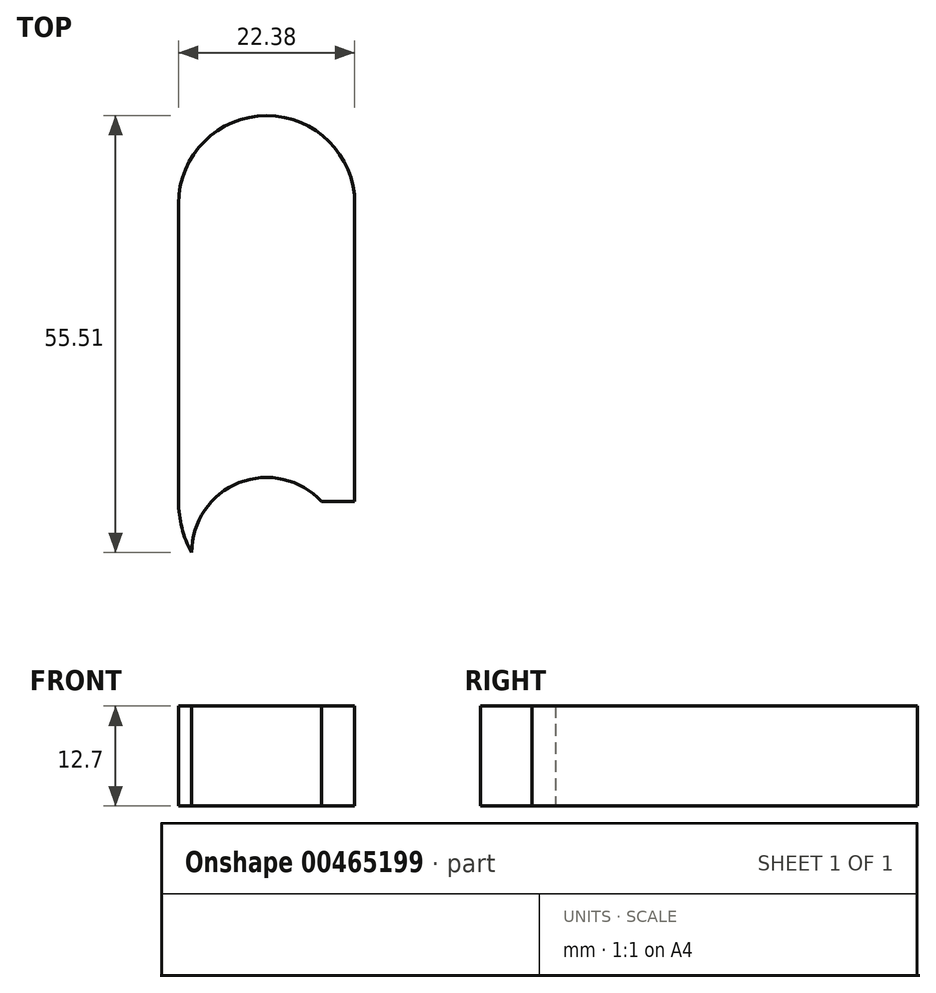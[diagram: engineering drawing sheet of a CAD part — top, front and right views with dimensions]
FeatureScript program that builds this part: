
annotation { "Feature Type Name" : "Feature", "Feature Type Description" : "" }
export const myFeature = defineFeature(function(context is Context, id is Id, definition is map)
    precondition{}
    {
        {
            var Q0;
            Q0=qCreatedBy(makeId("Top.planeOp"),FACE);
            var sketch = newSketch(context, id + "F0", { "sketchPlane" : qUnion([Q0])});
            skCircle(sketch, "E0", {"center": v(0, 0) * mm, "radius": 9.53 * mm});
            skLineSegment(sketch, "E1", {"start": v(0, 0) * mm, "end": v(0, 25.4) * mm});
            skLineSegment(sketch, "E2.bottom", {"start": v(11.2, 6.49) * mm, "end": v(-11.2, 6.49) * mm});
            skLineSegment(sketch, "E2.top", {"start": v(11.2, 44.31) * mm, "end": v(-11.2, 44.31) * mm});
            skLineSegment(sketch, "E2.left", {"start": v(11.2, 6.49) * mm, "end": v(11.2, 44.31) * mm});
            skLineSegment(sketch, "E2.right", {"start": v(-11.2, 6.49) * mm, "end": v(-11.2, 44.31) * mm});
            skPoint(sketch, "E2.middle", {"position": v(0, 25.4) * mm});
            skArc(sketch, "E3", {"start": v(-11.2, 44.31) * mm, "mid": v(0, 55.5) * mm, "end": v(11.2, 44.31) * mm});
            skArc(sketch, "E4", {"start": v(11.2, 6.49) * mm, "mid": v(10.77, 3.14) * mm, "end": v(9.53, 0) * mm});
            skArc(sketch, "E5", {"start": v(-11.2, 6.49) * mm, "mid": v(-10.77, 3.14) * mm, "end": v(-9.53, 0) * mm});
            skLineSegment(sketch, "E6", {"start": v(-8.84, -3.54) * mm, "end": v(-11.67, -9.3) * mm});
            skLineSegment(sketch, "E7", {"start": v(-11.67, -9.3) * mm, "end": v(-9.89, -15.42) * mm});
            skLineSegment(sketch, "E8", {"start": v(-9.89, -15.42) * mm, "end": v(-4.82, -8.22) * mm});
            skLineSegment(sketch, "E9", {"start": v(-4.82, -8.22) * mm, "end": v(4.82, -8.22) * mm});
            skLineSegment(sketch, "E10", {"start": v(4.82, -8.22) * mm, "end": v(7.67, -14.7) * mm});
            skLineSegment(sketch, "E11", {"start": v(7.67, -14.7) * mm, "end": v(11.12, -9.3) * mm});
            skLineSegment(sketch, "E12", {"start": v(11.12, -9.3) * mm, "end": v(9.53, 0) * mm});
            skLineSegment(sketch, "E13", {"start": v(-9.53, 0) * mm, "end": v(-11.67, -9.3) * mm});
            skSolve(sketch);
        }
        {
            var Q0;
            Q0=makeQuery(id+"F0.imprint","IMPRINT",FACE,{"disambiguationData":[TD([[makeQuery(id+"F0.imprint","IMPRINT",EDGE,{"derivedFrom":sQuery(id+"F0.wireOp",EDGE,"E2.top")}),-1.0]])]});
            var Q1;
            Q1=makeQuery(id+"F0.imprint","IMPRINT",FACE,{"disambiguationData":[TD([[makeQuery(id+"F0.imprint","IMPRINT",EDGE,{"derivedFrom":sQuery(id+"F0.wireOp",EDGE,"E2.top")}),1.0]])]});
            var Q2;
            {var subQ0=sQuery(id+"F0.wireOp",EDGE,"E4");Q2=makeQuery(id+"F0.imprint","IMPRINT",FACE,{"disambiguationData":[TD([[makeQuery(id+"F0.imprint","IMPRINT",EDGE,{"derivedFrom":subQ0}),-1.0]])]});}
            var Q3;
            {var subQ0=sQuery(id+"F0.wireOp",EDGE,"E5");Q3=makeQuery(id+"F0.imprint","IMPRINT",FACE,{"disambiguationData":[TD([[makeQuery(id+"F0.imprint","IMPRINT",EDGE,{"derivedFrom":subQ0}),1.0]])]});}
            extrude(context, id + "F1", {"entities" : qUnion([Q0, Q1, Q2, Q3]), "depth" : 12.7 * mm});
        }
    });
